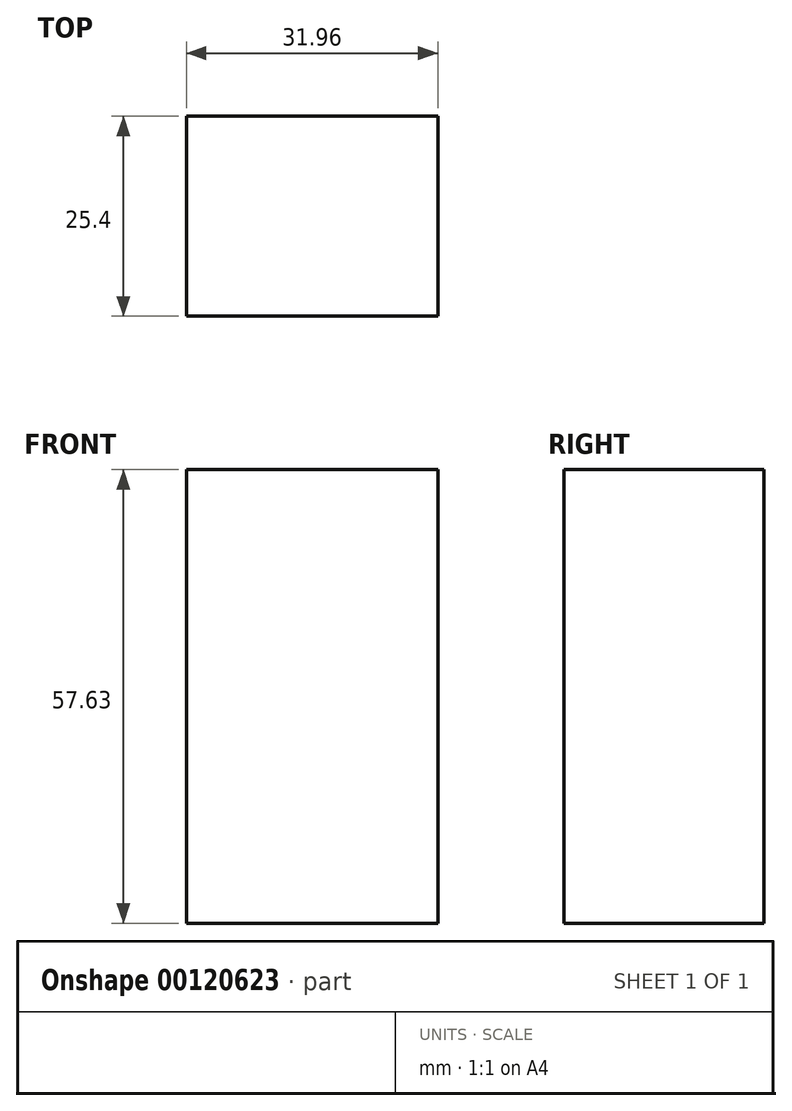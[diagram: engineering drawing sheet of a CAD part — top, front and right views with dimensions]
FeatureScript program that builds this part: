
annotation { "Feature Type Name" : "Feature", "Feature Type Description" : "" }
export const myFeature = defineFeature(function(context is Context, id is Id, definition is map)
    precondition{}
    {
        {
            var Q0;
            Q0=qCreatedBy(makeId("Front.planeOp"),FACE);
            var sketch = newSketch(context, id + "F0", { "sketchPlane" : qUnion([Q0])});
            skLineSegment(sketch, "E0.bottom", {"start": v(0, 0) * mm, "end": v(31.96, 0) * mm});
            skLineSegment(sketch, "E0.top", {"start": v(0, 57.63) * mm, "end": v(31.96, 57.63) * mm});
            skLineSegment(sketch, "E0.left", {"start": v(0, 0) * mm, "end": v(0, 57.63) * mm});
            skLineSegment(sketch, "E0.right", {"start": v(31.96, 0) * mm, "end": v(31.96, 57.63) * mm});
            skSolve(sketch);
        }
        {
            var Q0;
            Q0=makeQuery(id+"F0.imprint","IMPRINT",FACE,{"disambiguationData":[TD([[makeQuery(id+"F0.imprint","IMPRINT",EDGE,{"derivedFrom":sQuery(id+"F0.wireOp",EDGE,"E0.bottom")}),1.0]])]});
            var sketch = newSketch(context, id + "F1", { "sketchPlane" : qUnion([Q0])});
            skSolve(sketch);
        }
        {
            var Q0;
            Q0 = qSketchRegion(id + "F1", true);
            var Q1;
            Q1=makeQuery(id+"F0.imprint","IMPRINT",FACE,{"disambiguationData":[TD([[makeQuery(id+"F0.imprint","IMPRINT",EDGE,{"derivedFrom":sQuery(id+"F0.wireOp",EDGE,"E0.bottom")}),1.0]])]});
            extrude(context, id + "F2", {"entities" : qUnion([Q0, Q1]), "endBound" : BoundingType.SYMMETRIC, "depth" : 25.4 * mm});
        }
    });
